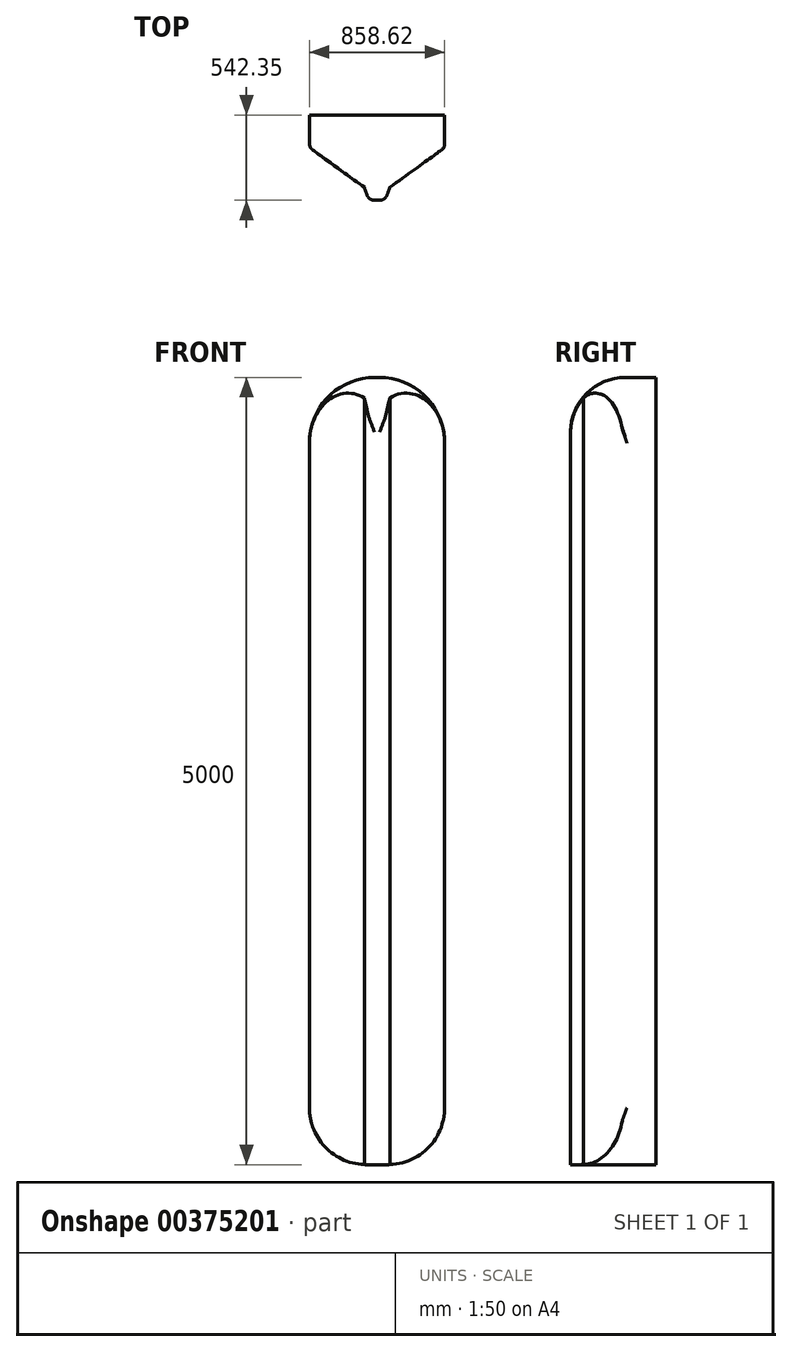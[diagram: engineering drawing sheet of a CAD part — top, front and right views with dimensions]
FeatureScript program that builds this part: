
annotation { "Feature Type Name" : "Feature", "Feature Type Description" : "" }
export const myFeature = defineFeature(function(context is Context, id is Id, definition is map)
    precondition{}
    {
        {
            var Q0;
            Q0=qCreatedBy(makeId("Top.planeOp"),FACE);
            var sketch = newSketch(context, id + "F0", { "sketchPlane" : qUnion([Q0])});
            skLineSegment(sketch, "E0", {"start": v(-61.12, -16.9) * mm, "end": v(-56.5, -23.84) * mm});
            skLineSegment(sketch, "E1", {"start": v(-40.47, -39.33) * mm, "end": v(286.97, -276.82) * mm});
            skLineSegment(sketch, "E2", {"start": v(286.97, -276.82) * mm, "end": v(304.75, -326.2) * mm});
            skLineSegment(sketch, "E3", {"start": v(351.8, -359.26) * mm, "end": v(368.2, -359.26) * mm});
            skLineSegment(sketch, "E4", {"start": v(368.2, -359.26) * mm, "end": v(368.2, 819.04) * mm});
            skLineSegment(sketch, "E5.MirrorCS", {"start": v(384.6, -359.26) * mm, "end": v(368.2, -359.26) * mm});
            skLineSegment(sketch, "E6.MirrorCS", {"start": v(449.42, -276.82) * mm, "end": v(431.64, -326.2) * mm});
            skLineSegment(sketch, "E7.MirrorCS", {"start": v(787.85, -31.36) * mm, "end": v(449.42, -276.82) * mm});
            skLineSegment(sketch, "E8.MirrorCS", {"start": v(789.12, -29.5) * mm, "end": v(787.94, -31.26) * mm});
            skPoint(sketch, "E9.MirrorCS.end.orphan", {"position": v(797.5, -16.9) * mm});
            skPoint(sketch, "E9.MirrorCS.start.orphan", {"position": v(797.5, 483.1) * mm});
            skPoint(sketch, "E10.start.orphan", {"position": v(-61.12, 483.1) * mm});
            skLineSegment(sketch, "E11", {"start": v(-61.12, 1.15) * mm, "end": v(-61.12, 183.1) * mm});
            skLineSegment(sketch, "E12", {"start": v(797.5, -1.78) * mm, "end": v(797.5, 183.1) * mm});
            skPoint(sketch, "E13.visualSharp", {"position": v(316.65, -359.26) * mm});
            skArc(sketch, "E13.filletArc", {"start": v(304.75, -326.2) * mm, "mid": v(323.04, -350.17) * mm, "end": v(351.8, -359.26) * mm});
            skPoint(sketch, "E14.visualSharp", {"position": v(419.74, -359.26) * mm});
            skArc(sketch, "E14.filletArc", {"start": v(384.6, -359.26) * mm, "mid": v(413.35, -350.17) * mm, "end": v(431.64, -326.2) * mm});
            skPoint(sketch, "E15.visualSharp", {"position": v(-51.52, -31.32) * mm});
            skArc(sketch, "E15.filletArc", {"start": v(-56.5, -23.84) * mm, "mid": v(-50.94, -30.76) * mm, "end": v(-44.24, -36.6) * mm});
            skPoint(sketch, "E16.newPointB", {"position": v(-61.12, -16.9) * mm});
            skArc(sketch, "E16.filletArc", {"start": v(-61.12, 1.15) * mm, "mid": v(-55.66, -21.57) * mm, "end": v(-40.47, -39.33) * mm});
            skArc(sketch, "E17.filletArc", {"start": v(789.12, -29.5) * mm, "mid": v(795.36, -16.26) * mm, "end": v(797.5, -1.78) * mm});
            skPoint(sketch, "E18.visualSharp", {"position": v(787.9, -31.32) * mm});
            skArc(sketch, "E18.filletArc", {"start": v(787.85, -31.36) * mm, "mid": v(787.9, -31.31) * mm, "end": v(787.94, -31.26) * mm});
            skLineSegment(sketch, "E19", {"start": v(-61.12, 183.1) * mm, "end": v(797.5, 183.1) * mm});
            skSolve(sketch);
        }
        {
            var Q0;
            Q0=makeQuery(id+"F0.imprint","IMPRINT",FACE,{"disambiguationData":[TD([[makeQuery(id+"F0.imprint","IMPRINT",EDGE,{"derivedFrom":sQuery(id+"F0.wireOp",EDGE,"E1")}),1.0]])]});
            var Q1;
            {var subQ4=sQuery(id+"F0.wireOp",EDGE,"E5.MirrorCS");Q1=makeQuery(id+"F0.imprint","IMPRINT",FACE,{"disambiguationData":[TD([[makeQuery(id+"F0.imprint","IMPRINT",EDGE,{"derivedFrom":subQ4}),-1.0]])]});}
            extrude(context, id + "F1", {"entities" : qUnion([Q0, Q1]), "depth" : 5000 * mm});
        }
        {
            var Q0;
            Q0=makeQuery(id+"F1.opExtrude","CAP_EDGE",EDGE,{"disambiguationData":[OSD([sQuery(id+"F0.wireOp",EDGE,"E7.MirrorCS")])],"isStart":false});
            fillet(context, id + "F2", {"entities" : qUnion([Q0]), "radius" : 415.24 * mm, "tangentPropagation" : true, "allowEdgeOverflow" : false});
        }
        {
            var Q0;
            Q0=makeQuery(id+"F1.opExtrude","CAP_EDGE",EDGE,{"disambiguationData":[OSD([sQuery(id+"F0.wireOp",EDGE,"E1")])],"isStart":false});
            fillet(context, id + "F3", {"entities" : qUnion([Q0]), "radius" : 415.25 * mm, "tangentPropagation" : true, "allowEdgeOverflow" : false});
        }
        {
            var Q0;
            Q0=makeQuery(id+"F1.opExtrude","CAP_EDGE",EDGE,{"disambiguationData":[OSD([sQuery(id+"F0.wireOp",EDGE,"E3"),sQuery(id+"F0.wireOp",EDGE,"E5.MirrorCS")])],"isStart":false});
            fillet(context, id + "F4", {"entities" : qUnion([Q0]), "radius" : 347.65 * mm, "tangentPropagation" : true, "allowEdgeOverflow" : false});
        }
        {
            var Q0;
            Q0=makeQuery(id+"F1.opExtrude","CAP_EDGE",EDGE,{"disambiguationData":[OSD([sQuery(id+"F0.wireOp",EDGE,"E1")])],"isStart":true});
            var Q1;
            Q1=makeQuery(id+"F1.opExtrude","CAP_EDGE",EDGE,{"disambiguationData":[OSD([sQuery(id+"F0.wireOp",EDGE,"E7.MirrorCS")])],"isStart":true});
            fillet(context, id + "F5", {"entities" : qUnion([Q0, Q1]), "radius" : 359.72 * mm, "tangentPropagation" : true, "allowEdgeOverflow" : false});
        }
    });
